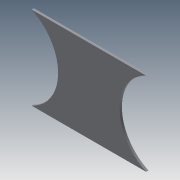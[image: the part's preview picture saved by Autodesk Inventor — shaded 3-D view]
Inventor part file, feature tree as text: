
AUTODESK INVENTOR PART (.ipt)
format: ipt  version: 2013 (Build 170138000, 138)  size: 73,216 bytes
history: native  units: mm
features: extrude x1, sketch x1
ambient origin geometry x8: Origin, YZ Plane, XZ Plane, XY Plane, X Axis, Y Axis, Z Axis, Center Point
bodies: Solid1 (feature_tree)
feature tree (2):
  extrude  "Extrusion1"  Depth=72.6mm
  sketch  "Sketch1"  dims[d0=100.0mm d1=72.6mm d4=40.0mm d5=40.0mm d6=2.0mm d7=0.0mm]
